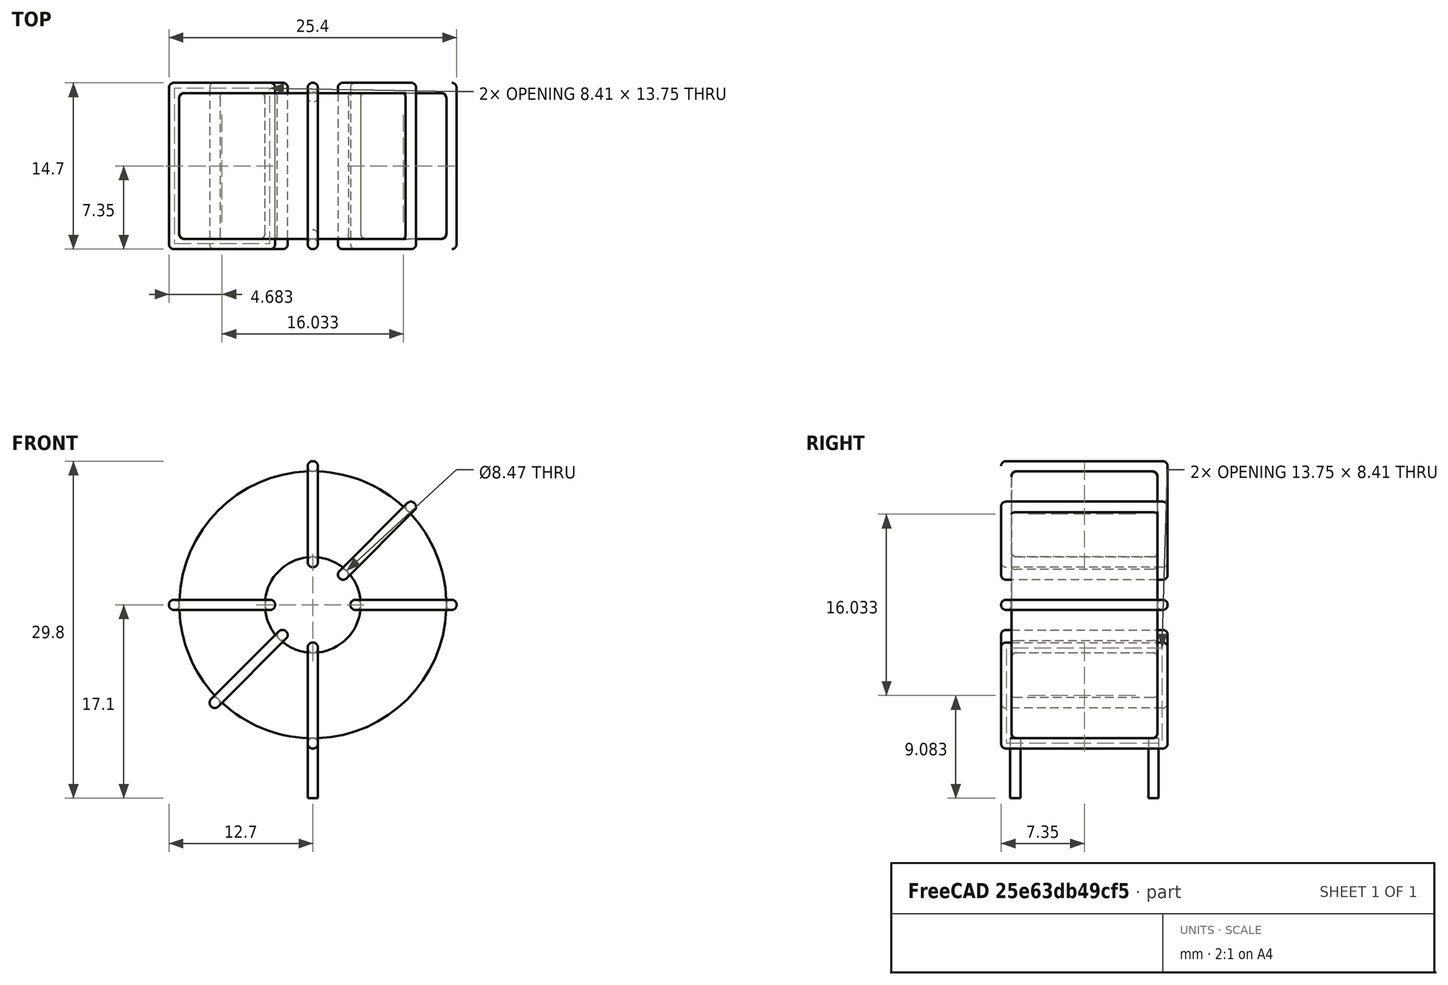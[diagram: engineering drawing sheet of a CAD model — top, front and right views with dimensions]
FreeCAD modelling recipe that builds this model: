
FCSTD DOCUMENT  (FreeCAD 0.16R6703 (Git))
Label: L_Toroid_Vertical_L25.4mm_W14.7mm_P12.20mm_Vishay_TJ5
License: All rights reserved
LicenseURL: http://en.wikipedia.org/wiki/All_rights_reserved
objects: Sketcher::SketchObject×6, PartDesign::Pad×6, PartDesign::Fillet×5, Spreadsheet::Sheet×1
note: 23 computed .brp shape members not serialized (recipe doc carries the construction recipe); baked Part::Feature solids carry a one-line shape summary decoded from their .brp

FEATURE [Spreadsheet::Sheet] Spreadsheet  label="dimensions"
  cells = A1=Wx; B1(Wx)=25.4; C1(WW)=8.466666666666667; D1=25.4; A2=Wy; B2(Wy)=14.7; D2=14.7; A3=RM; B3(RMx)=12.2; C3(RMy)=0; A4=d_wire; B4(d_wire)=0.8999999999999999; A5=H; B5(H)=25.4; A6=offsetx; B6(offsetx)=12.7
FEATURE [Sketcher::SketchObject] Sketch
  Placement = pos=(0,-6.1,0) rot=(1,0,0;1.5708rad)
  expr: Placement.Base.y = -Spreadsheet.RMx / 2
  expr: Constraints[0] = Spreadsheet.Wx / 2 - Spreadsheet.d_wire
  expr: Constraints[4] = Spreadsheet.WW / 2
  expr: Constraints[2] = Spreadsheet.Wx / 2 + Spreadsheet.d_wire + 0.5
  sketch-geometry (2):
    g0: Circle CenterX=0 CenterY=14.1 CenterZ=0 NormalX=0 NormalY=0 NormalZ=1 Radius=11.8
    g1: Circle CenterX=0 CenterY=14.1 CenterZ=0 NormalX=0 NormalY=0 NormalZ=1 Radius=4.23333
  constraints (5):
    c: Radius(g0) = 11.8
    c: DistanceX(g-1,g0) = 0
    c: DistanceY(g-1,g0) = 14.1
    c: Coincident(g1,g0)
    c: Radius(g1) = 4.23333
FEATURE [PartDesign::Pad] Pad
  Length = 12.9
  Length2 = 100
  Midplane = true
  Placement = pos=(0,-6.1,0) rot=(1,0,0;1.5708rad)
  Sketch = -> Sketch
  Type = 0
  expr: Length = Spreadsheet.Wy - 2 * Spreadsheet.d_wire
FEATURE [Sketcher::SketchObject] Sketch001
  Placement = pos=(0,0,1.4) rot=(0,0,1;0rad)
  expr: Placement.Base.z = 0.5 + Spreadsheet.d_wire
  expr: Constraints[4] = Spreadsheet.RMy
  expr: Constraints[2] = -Spreadsheet.RMx
  expr: Constraints[1] = Spreadsheet.d_wire / 2
  sketch-geometry (2):
    g0: Circle CenterX=0 CenterY=0 CenterZ=0 NormalX=0 NormalY=0 NormalZ=1 Radius=0.45
    g1: Circle CenterX=0 CenterY=-12.2 CenterZ=0 NormalX=0 NormalY=0 NormalZ=1 Radius=0.45
  constraints (5):
    c: Equal(g0,g1)
    c: Radius(g0) = 0.45
    c: DistanceY(g-1,g1) = -12.2
    c: Coincident(g0,g-1)
    c: DistanceX(g-1,g1) = 0
FEATURE [PartDesign::Pad] Pad001
  Length = 0.9
  Length2 = 4.4
  Placement = pos=(0,0,1.4) rot=(0,0,1;0rad)
  Reversed = true
  Sketch = -> Sketch001
  Type = 4
  expr: Length2 = 3.5 + Spreadsheet.d_wire
  expr: Length = Spreadsheet.d_wire
FEATURE [PartDesign::Fillet] Fillet
  Base = -> Pad [Edge6,Edge3,Edge2]
  Placement = pos=(0,-6.1,0) rot=(1,0,0;1.5708rad)
  Radius = 0.5
FEATURE [Sketcher::SketchObject] Sketch003
  Placement = pos=(0,1.25,14.1) rot=(1,0,0;3.14159rad)
  expr: Constraints[18] = Spreadsheet.d_wire
  expr: Constraints[16] = Spreadsheet.d_wire
  expr: Constraints[19] = Spreadsheet.d_wire
  expr: Constraints[17] = Spreadsheet.d_wire
  expr: Placement.Base.y = -1 * (Spreadsheet.RMx - Spreadsheet.Wy) / 2
  expr: Constraints[21] = (Spreadsheet.Wx - Spreadsheet.WW) / 2 - Spreadsheet.d_wire
  expr: Constraints[22] = Spreadsheet.Wx / 2 - Spreadsheet.d_wire
  expr: Constraints[43] = Spreadsheet.d_wire
  expr: Constraints[48] = Spreadsheet.Wx - Spreadsheet.d_wire * 2
  expr: Constraints[49] = Spreadsheet.Wy
  expr: Placement.Base.z = Spreadsheet.Wx / 2 + Spreadsheet.d_wire + 0.5
  sketch-geometry (16):
    g0: LineSegment StartX=-3.33333 StartY=0 StartZ=0 EndX=-12.7 EndY=0 EndZ=0
    g1: LineSegment StartX=-12.7 StartY=0 StartZ=0 EndX=-12.7 EndY=14.7 EndZ=0
    g2: LineSegment StartX=-12.7 StartY=14.7 StartZ=0 EndX=-3.33333 EndY=14.7 EndZ=0
    g3: LineSegment StartX=-3.33333 StartY=14.7 StartZ=0 EndX=-3.33333 EndY=0 EndZ=0
    g4: LineSegment StartX=-11.8 StartY=13.8 StartZ=0 EndX=-4.23333 EndY=13.8 EndZ=0
    g5: LineSegment StartX=-4.23333 StartY=13.8 StartZ=0 EndX=-4.23333 EndY=0.9 EndZ=0
    g6: LineSegment StartX=-4.23333 StartY=0.9 StartZ=0 EndX=-11.8 EndY=0.9 EndZ=0
    g7: LineSegment StartX=-11.8 StartY=0.9 StartZ=0 EndX=-11.8 EndY=13.8 EndZ=0
    g8: LineSegment StartX=3.33333 StartY=14.7 StartZ=0 EndX=12.7 EndY=14.7 EndZ=0
    g9: LineSegment StartX=12.7 StartY=14.7 StartZ=0 EndX=12.7 EndY=0 EndZ=0
    g10: LineSegment StartX=12.7 StartY=0 StartZ=0 EndX=3.33333 EndY=0 EndZ=0
    g11: LineSegment StartX=3.33333 StartY=0 StartZ=0 EndX=3.33333 EndY=14.7 EndZ=0
    g12: LineSegment StartX=4.23333 StartY=13.8 StartZ=0 EndX=11.8 EndY=13.8 EndZ=0
    g13: LineSegment StartX=11.8 StartY=13.8 StartZ=0 EndX=11.8 EndY=0.9 EndZ=0
    g14: LineSegment StartX=11.8 StartY=0.9 StartZ=0 EndX=4.23333 EndY=0.9 EndZ=0
    g15: LineSegment StartX=4.23333 StartY=0.9 StartZ=0 EndX=4.23333 EndY=13.8 EndZ=0
  constraints (50):
    c: Horizontal(g0)
    c: Coincident(g1,g0)
    c: Vertical(g1)
    c: Coincident(g2,g1)
    c: Horizontal(g2)
    c: Coincident(g3,g2)
    c: Coincident(g3,g0)
    c: Vertical(g3)
    c: Coincident(g4,g5)
    c: Coincident(g5,g6)
    c: Coincident(g6,g7)
    c: Coincident(g7,g4)
    c: Horizontal(g4)
    c: Horizontal(g6)
    c: Vertical(g5)
    c: Vertical(g7)
    c: DistanceX(g1,g4) = 0.9
    c: DistanceY(g4,g1) = 0.9
    c: DistanceX(g5,g0) = 0.9
    c: DistanceY(g0,g5) = 0.9
    c: DistanceY(g-1,g0) = 0
    c: DistanceX(g6,g6) = 7.56667
    c: DistanceX(g6,g-1) = 11.8
    c: Coincident(g8,g9)
    c: Coincident(g9,g10)
    c: Coincident(g10,g11)
    c: Coincident(g11,g8)
    c: Horizontal(g8)
    c: Horizontal(g10)
    c: Vertical(g9)
    c: Vertical(g11)
    c: Coincident(g12,g13)
    c: Coincident(g13,g14)
    c: Coincident(g14,g15)
    c: Coincident(g15,g12)
    c: Horizontal(g12)
    c: Horizontal(g14)
    c: Vertical(g13)
    c: Vertical(g15)
    c: DistanceY(g8,g2) = 0
    c: DistanceY(g10,g0) = 0
    c: DistanceY(g14,g5) = 0
    c: DistanceY(g12,g4) = 0
    c: DistanceX(g8,g12) = 0.9
    c: Equal(g8,g2)
    c: Equal(g12,g4)
    c: Equal(g9,g1)
    c: Equal(g13,g7)
    c: DistanceX(g4,g12) = 23.6
    c: DistanceY(g0,g1) = 14.7
FEATURE [PartDesign::Pad] Pad002
  Length = 0.9
  Length2 = 100
  Midplane = true
  Placement = pos=(0,1.25,14.1) rot=(1,0,0;3.14159rad)
  Sketch = -> Sketch003
  Type = 0
  expr: Length = Spreadsheet.d_wire
FEATURE [PartDesign::Fillet] Fillet001
  Base = -> Pad002 [Edge38,Edge41,Edge42,Edge43,Edge29,Edge32,Edge33,Edge34,Edge25,Edge35,Edge36,Edge13,Edge14,Edge15,Edge16,Edge17,Edge18,Edge19,Edge1,Edge2,Edge3,Edge4,Edge5,Edge6,Edge7,Edge37,Edge39,Edge40,Edge20,Edge23,Edge24,Edge21,Edge22,Edge8,Edge9,Edge10,Edge11,Edge12,Edge26,Edge27,+8 more]
  Placement = pos=(0,1.25,14.1) rot=(1,0,0;3.14159rad)
  Radius = 0.423
  expr: Radius = Spreadsheet.d_wire * 0.47
FEATURE [Sketcher::SketchObject] Sketch004
  Placement = pos=(0,1.25,14.1) rot=(0.92388,0,0.382683;3.14159rad)
  expr: Constraints[18] = Spreadsheet.d_wire
  expr: Constraints[16] = Spreadsheet.d_wire
  expr: Constraints[19] = Spreadsheet.d_wire
  expr: Constraints[17] = Spreadsheet.d_wire
  expr: Placement.Base.y = -1 * (Spreadsheet.RMx - Spreadsheet.Wy) / 2
  expr: Constraints[21] = (Spreadsheet.Wx - Spreadsheet.WW) / 2 - Spreadsheet.d_wire
  expr: Constraints[22] = Spreadsheet.Wx / 2 - Spreadsheet.d_wire
  expr: Constraints[43] = Spreadsheet.d_wire
  expr: Constraints[48] = Spreadsheet.Wx - 2 * Spreadsheet.d_wire
  expr: Constraints[49] = Spreadsheet.Wy
  expr: Placement.Base.z = Spreadsheet.Wx / 2 + Spreadsheet.d_wire + 0.5
  sketch-geometry (16):
    g0: LineSegment StartX=-3.33333 StartY=0 StartZ=0 EndX=-12.7 EndY=0 EndZ=0
    g1: LineSegment StartX=-12.7 StartY=0 StartZ=0 EndX=-12.7 EndY=14.7 EndZ=0
    g2: LineSegment StartX=-12.7 StartY=14.7 StartZ=0 EndX=-3.33333 EndY=14.7 EndZ=0
    g3: LineSegment StartX=-3.33333 StartY=14.7 StartZ=0 EndX=-3.33333 EndY=0 EndZ=0
    g4: LineSegment StartX=-11.8 StartY=13.8 StartZ=0 EndX=-4.23333 EndY=13.8 EndZ=0
    g5: LineSegment StartX=-4.23333 StartY=13.8 StartZ=0 EndX=-4.23333 EndY=0.9 EndZ=0
    g6: LineSegment StartX=-4.23333 StartY=0.9 StartZ=0 EndX=-11.8 EndY=0.9 EndZ=0
    g7: LineSegment StartX=-11.8 StartY=0.9 StartZ=0 EndX=-11.8 EndY=13.8 EndZ=0
    g8: LineSegment StartX=3.33333 StartY=14.7 StartZ=0 EndX=12.7 EndY=14.7 EndZ=0
    g9: LineSegment StartX=12.7 StartY=14.7 StartZ=0 EndX=12.7 EndY=0 EndZ=0
    g10: LineSegment StartX=12.7 StartY=0 StartZ=0 EndX=3.33333 EndY=0 EndZ=0
    g11: LineSegment StartX=3.33333 StartY=0 StartZ=0 EndX=3.33333 EndY=14.7 EndZ=0
    g12: LineSegment StartX=4.23333 StartY=13.8 StartZ=0 EndX=11.8 EndY=13.8 EndZ=0
    g13: LineSegment StartX=11.8 StartY=13.8 StartZ=0 EndX=11.8 EndY=0.9 EndZ=0
    g14: LineSegment StartX=11.8 StartY=0.9 StartZ=0 EndX=4.23333 EndY=0.9 EndZ=0
    g15: LineSegment StartX=4.23333 StartY=0.9 StartZ=0 EndX=4.23333 EndY=13.8 EndZ=0
  constraints (50):
    c: Horizontal(g0)
    c: Coincident(g1,g0)
    c: Vertical(g1)
    c: Coincident(g2,g1)
    c: Horizontal(g2)
    c: Coincident(g3,g2)
    c: Coincident(g3,g0)
    c: Vertical(g3)
    c: Coincident(g4,g5)
    c: Coincident(g5,g6)
    c: Coincident(g6,g7)
    c: Coincident(g7,g4)
    c: Horizontal(g4)
    c: Horizontal(g6)
    c: Vertical(g5)
    c: Vertical(g7)
    c: DistanceX(g1,g4) = 0.9
    c: DistanceY(g4,g1) = 0.9
    c: DistanceX(g5,g0) = 0.9
    c: DistanceY(g0,g5) = 0.9
    c: DistanceY(g-1,g0) = 0
    c: DistanceX(g6,g6) = 7.56667
    c: DistanceX(g6,g-1) = 11.8
    c: Coincident(g8,g9)
    c: Coincident(g9,g10)
    c: Coincident(g10,g11)
    c: Coincident(g11,g8)
    c: Horizontal(g8)
    c: Horizontal(g10)
    c: Vertical(g9)
    c: Vertical(g11)
    c: Coincident(g12,g13)
    c: Coincident(g13,g14)
    c: Coincident(g14,g15)
    c: Coincident(g15,g12)
    c: Horizontal(g12)
    c: Horizontal(g14)
    c: Vertical(g13)
    c: Vertical(g15)
    c: DistanceY(g8,g2) = 0
    c: DistanceY(g10,g0) = 0
    c: DistanceY(g14,g5) = 0
    c: DistanceY(g12,g4) = 0
    c: DistanceX(g8,g12) = 0.9
    c: Equal(g8,g2)
    c: Equal(g12,g4)
    c: Equal(g9,g1)
    c: Equal(g13,g7)
    c: DistanceX(g4,g12) = 23.6
    c: DistanceY(g0,g1) = 14.7
FEATURE [PartDesign::Pad] Pad003
  Length = 0.9
  Length2 = 100
  Midplane = true
  Placement = pos=(0,1.25,14.1) rot=(0.92388,0,0.382683;3.14159rad)
  Sketch = -> Sketch004
  Type = 0
  expr: Length = Spreadsheet.d_wire
FEATURE [PartDesign::Fillet] Fillet002
  Base = -> Pad003 [Edge38,Edge41,Edge42,Edge43,Edge29,Edge32,Edge33,Edge34,Edge25,Edge35,Edge36,Edge13,Edge14,Edge15,Edge16,Edge17,Edge18,Edge19,Edge1,Edge2,Edge3,Edge4,Edge5,Edge6,Edge7,Edge37,Edge39,Edge40,Edge20,Edge23,Edge24,Edge21,Edge22,Edge8,Edge9,Edge10,Edge11,Edge12,Edge26,Edge27,+8 more]
  Placement = pos=(0,1.25,14.1) rot=(0.92388,0,0.382683;3.14159rad)
  Radius = 0.423
  expr: Radius = Spreadsheet.d_wire * 0.47
FEATURE [Sketcher::SketchObject] Sketch005
  Placement = pos=(0,1.25,14.1) rot=(0.92388,0,-0.382683;3.14159rad)
  expr: Constraints[18] = Spreadsheet.d_wire
  expr: Constraints[16] = Spreadsheet.d_wire
  expr: Constraints[19] = Spreadsheet.d_wire
  expr: Constraints[17] = Spreadsheet.d_wire
  expr: Placement.Base.y = -1 * (Spreadsheet.RMx - Spreadsheet.Wy) / 2
  expr: Constraints[21] = (Spreadsheet.Wx - Spreadsheet.WW) / 2 - Spreadsheet.d_wire
  expr: Constraints[22] = Spreadsheet.Wx / 2 - Spreadsheet.d_wire
  expr: Constraints[43] = Spreadsheet.d_wire
  expr: Constraints[48] = Spreadsheet.Wx - 2 * Spreadsheet.d_wire
  expr: Constraints[49] = Spreadsheet.Wy
  expr: Placement.Base.z = Spreadsheet.Wx / 2 + Spreadsheet.d_wire + 0.5
  sketch-geometry (16):
    g0: LineSegment StartX=-3.33333 StartY=0 StartZ=0 EndX=-12.7 EndY=0 EndZ=0
    g1: LineSegment StartX=-12.7 StartY=0 StartZ=0 EndX=-12.7 EndY=14.7 EndZ=0
    g2: LineSegment StartX=-12.7 StartY=14.7 StartZ=0 EndX=-3.33333 EndY=14.7 EndZ=0
    g3: LineSegment StartX=-3.33333 StartY=14.7 StartZ=0 EndX=-3.33333 EndY=0 EndZ=0
    g4: LineSegment StartX=-11.8 StartY=13.8 StartZ=0 EndX=-4.23333 EndY=13.8 EndZ=0
    g5: LineSegment StartX=-4.23333 StartY=13.8 StartZ=0 EndX=-4.23333 EndY=0.9 EndZ=0
    g6: LineSegment StartX=-4.23333 StartY=0.9 StartZ=0 EndX=-11.8 EndY=0.9 EndZ=0
    g7: LineSegment StartX=-11.8 StartY=0.9 StartZ=0 EndX=-11.8 EndY=13.8 EndZ=0
    g8: LineSegment StartX=3.33333 StartY=14.7 StartZ=0 EndX=12.7 EndY=14.7 EndZ=0
    g9: LineSegment StartX=12.7 StartY=14.7 StartZ=0 EndX=12.7 EndY=0 EndZ=0
    g10: LineSegment StartX=12.7 StartY=0 StartZ=0 EndX=3.33333 EndY=0 EndZ=0
    g11: LineSegment StartX=3.33333 StartY=0 StartZ=0 EndX=3.33333 EndY=14.7 EndZ=0
    g12: LineSegment StartX=4.23333 StartY=13.8 StartZ=0 EndX=11.8 EndY=13.8 EndZ=0
    g13: LineSegment StartX=11.8 StartY=13.8 StartZ=0 EndX=11.8 EndY=0.9 EndZ=0
    g14: LineSegment StartX=11.8 StartY=0.9 StartZ=0 EndX=4.23333 EndY=0.9 EndZ=0
    g15: LineSegment StartX=4.23333 StartY=0.9 StartZ=0 EndX=4.23333 EndY=13.8 EndZ=0
  constraints (50):
    c: Horizontal(g0)
    c: Coincident(g1,g0)
    c: Vertical(g1)
    c: Coincident(g2,g1)
    c: Horizontal(g2)
    c: Coincident(g3,g2)
    c: Coincident(g3,g0)
    c: Vertical(g3)
    c: Coincident(g4,g5)
    c: Coincident(g5,g6)
    c: Coincident(g6,g7)
    c: Coincident(g7,g4)
    c: Horizontal(g4)
    c: Horizontal(g6)
    c: Vertical(g5)
    c: Vertical(g7)
    c: DistanceX(g1,g4) = 0.9
    c: DistanceY(g4,g1) = 0.9
    c: DistanceX(g5,g0) = 0.9
    c: DistanceY(g0,g5) = 0.9
    c: DistanceY(g-1,g0) = 0
    c: DistanceX(g6,g6) = 7.56667
    c: DistanceX(g6,g-1) = 11.8
    c: Coincident(g8,g9)
    c: Coincident(g9,g10)
    c: Coincident(g10,g11)
    c: Coincident(g11,g8)
    c: Horizontal(g8)
    c: Horizontal(g10)
    c: Vertical(g9)
    c: Vertical(g11)
    c: Coincident(g12,g13)
    c: Coincident(g13,g14)
    c: Coincident(g14,g15)
    c: Coincident(g15,g12)
    c: Horizontal(g12)
    c: Horizontal(g14)
    c: Vertical(g13)
    c: Vertical(g15)
    c: DistanceY(g8,g2) = 0
    c: DistanceY(g10,g0) = 0
    c: DistanceY(g14,g5) = 0
    c: DistanceY(g12,g4) = 0
    c: DistanceX(g8,g12) = 0.9
    c: Equal(g8,g2)
    c: Equal(g12,g4)
    c: Equal(g9,g1)
    c: Equal(g13,g7)
    c: DistanceX(g4,g12) = 23.6
    c: DistanceY(g0,g1) = 14.7
FEATURE [PartDesign::Pad] Pad004
  Length = 0.9
  Length2 = 100
  Midplane = true
  Placement = pos=(0,1.25,14.1) rot=(0.92388,0,-0.382683;3.14159rad)
  Sketch = -> Sketch005
  Type = 0
  expr: Length = Spreadsheet.d_wire
FEATURE [PartDesign::Fillet] Fillet003
  Base = -> Pad004 [Edge38,Edge41,Edge42,Edge43,Edge29,Edge32,Edge33,Edge34,Edge25,Edge35,Edge36,Edge13,Edge14,Edge15,Edge16,Edge17,Edge18,Edge19,Edge1,Edge2,Edge3,Edge4,Edge5,Edge6,Edge7,Edge37,Edge39,Edge40,Edge20,Edge23,Edge24,Edge21,Edge22,Edge8,Edge9,Edge10,Edge11,Edge12,Edge26,Edge27,+8 more]
  Placement = pos=(0,1.25,14.1) rot=(0.92388,0,-0.382683;3.14159rad)
  Radius = 0.423
  expr: Radius = Spreadsheet.d_wire * 0.47
FEATURE [Sketcher::SketchObject] Sketch006
  Placement = pos=(0,1.25,14.1) rot=(0.707107,0,0.707107;3.14159rad)
  expr: Constraints[18] = Spreadsheet.d_wire
  expr: Constraints[16] = Spreadsheet.d_wire
  expr: Constraints[19] = Spreadsheet.d_wire
  expr: Constraints[17] = Spreadsheet.d_wire
  expr: Placement.Base.y = -1 * (Spreadsheet.RMx - Spreadsheet.Wy) / 2
  expr: Constraints[21] = (Spreadsheet.Wx - Spreadsheet.WW) / 2 - Spreadsheet.d_wire
  expr: Constraints[22] = Spreadsheet.Wx / 2 - Spreadsheet.d_wire
  expr: Constraints[43] = Spreadsheet.d_wire
  expr: Constraints[48] = Spreadsheet.Wx - Spreadsheet.d_wire * 2
  expr: Constraints[49] = Spreadsheet.Wy
  expr: Placement.Base.z = Spreadsheet.Wx / 2 + Spreadsheet.d_wire + 0.5
  sketch-geometry (16):
    g0: LineSegment StartX=-3.33333 StartY=0 StartZ=0 EndX=-12.7 EndY=0 EndZ=0
    g1: LineSegment StartX=-12.7 StartY=0 StartZ=0 EndX=-12.7 EndY=14.7 EndZ=0
    g2: LineSegment StartX=-12.7 StartY=14.7 StartZ=0 EndX=-3.33333 EndY=14.7 EndZ=0
    g3: LineSegment StartX=-3.33333 StartY=14.7 StartZ=0 EndX=-3.33333 EndY=0 EndZ=0
    g4: LineSegment StartX=-11.8 StartY=13.8 StartZ=0 EndX=-4.23333 EndY=13.8 EndZ=0
    g5: LineSegment StartX=-4.23333 StartY=13.8 StartZ=0 EndX=-4.23333 EndY=0.9 EndZ=0
    g6: LineSegment StartX=-4.23333 StartY=0.9 StartZ=0 EndX=-11.8 EndY=0.9 EndZ=0
    g7: LineSegment StartX=-11.8 StartY=0.9 StartZ=0 EndX=-11.8 EndY=13.8 EndZ=0
    g8: LineSegment StartX=3.33333 StartY=14.7 StartZ=0 EndX=12.7 EndY=14.7 EndZ=0
    g9: LineSegment StartX=12.7 StartY=14.7 StartZ=0 EndX=12.7 EndY=0 EndZ=0
    g10: LineSegment StartX=12.7 StartY=0 StartZ=0 EndX=3.33333 EndY=0 EndZ=0
    g11: LineSegment StartX=3.33333 StartY=0 StartZ=0 EndX=3.33333 EndY=14.7 EndZ=0
    g12: LineSegment StartX=4.23333 StartY=13.8 StartZ=0 EndX=11.8 EndY=13.8 EndZ=0
    g13: LineSegment StartX=11.8 StartY=13.8 StartZ=0 EndX=11.8 EndY=0.9 EndZ=0
    g14: LineSegment StartX=11.8 StartY=0.9 StartZ=0 EndX=4.23333 EndY=0.9 EndZ=0
    g15: LineSegment StartX=4.23333 StartY=0.9 StartZ=0 EndX=4.23333 EndY=13.8 EndZ=0
  constraints (50):
    c: Horizontal(g0)
    c: Coincident(g1,g0)
    c: Vertical(g1)
    c: Coincident(g2,g1)
    c: Horizontal(g2)
    c: Coincident(g3,g2)
    c: Coincident(g3,g0)
    c: Vertical(g3)
    c: Coincident(g4,g5)
    c: Coincident(g5,g6)
    c: Coincident(g6,g7)
    c: Coincident(g7,g4)
    c: Horizontal(g4)
    c: Horizontal(g6)
    c: Vertical(g5)
    c: Vertical(g7)
    c: DistanceX(g1,g4) = 0.9
    c: DistanceY(g4,g1) = 0.9
    c: DistanceX(g5,g0) = 0.9
    c: DistanceY(g0,g5) = 0.9
    c: DistanceY(g-1,g0) = 0
    c: DistanceX(g6,g6) = 7.56667
    c: DistanceX(g6,g-1) = 11.8
    c: Coincident(g8,g9)
    c: Coincident(g9,g10)
    c: Coincident(g10,g11)
    c: Coincident(g11,g8)
    c: Horizontal(g8)
    c: Horizontal(g10)
    c: Vertical(g9)
    c: Vertical(g11)
    c: Coincident(g12,g13)
    c: Coincident(g13,g14)
    c: Coincident(g14,g15)
    c: Coincident(g15,g12)
    c: Horizontal(g12)
    c: Horizontal(g14)
    c: Vertical(g13)
    c: Vertical(g15)
    c: DistanceY(g8,g2) = 0
    c: DistanceY(g10,g0) = 0
    c: DistanceY(g14,g5) = 0
    c: DistanceY(g12,g4) = 0
    c: DistanceX(g8,g12) = 0.9
    c: Equal(g8,g2)
    c: Equal(g12,g4)
    c: Equal(g9,g1)
    c: Equal(g13,g7)
    c: DistanceX(g4,g12) = 23.6
    c: DistanceY(g0,g1) = 14.7
FEATURE [PartDesign::Pad] Pad005
  Length = 0.9
  Length2 = 100
  Midplane = true
  Placement = pos=(0,1.25,14.1) rot=(0.707107,0,0.707107;3.14159rad)
  Sketch = -> Sketch006
  Type = 0
  expr: Length = Spreadsheet.d_wire
FEATURE [PartDesign::Fillet] Fillet004
  Base = -> Pad005 [Edge38,Edge41,Edge42,Edge43,Edge29,Edge32,Edge33,Edge34,Edge25,Edge35,Edge36,Edge13,Edge14,Edge15,Edge16,Edge17,Edge18,Edge19,Edge1,Edge2,Edge3,Edge4,Edge5,Edge6,Edge7,Edge37,Edge39,Edge40,Edge20,Edge23,Edge24,Edge21,Edge22,Edge8,Edge9,Edge10,Edge11,Edge12,Edge26,Edge27,+8 more]
  Placement = pos=(0,1.25,14.1) rot=(0.707107,0,0.707107;3.14159rad)
  Radius = 0.423
  expr: Radius = Spreadsheet.d_wire * 0.47
